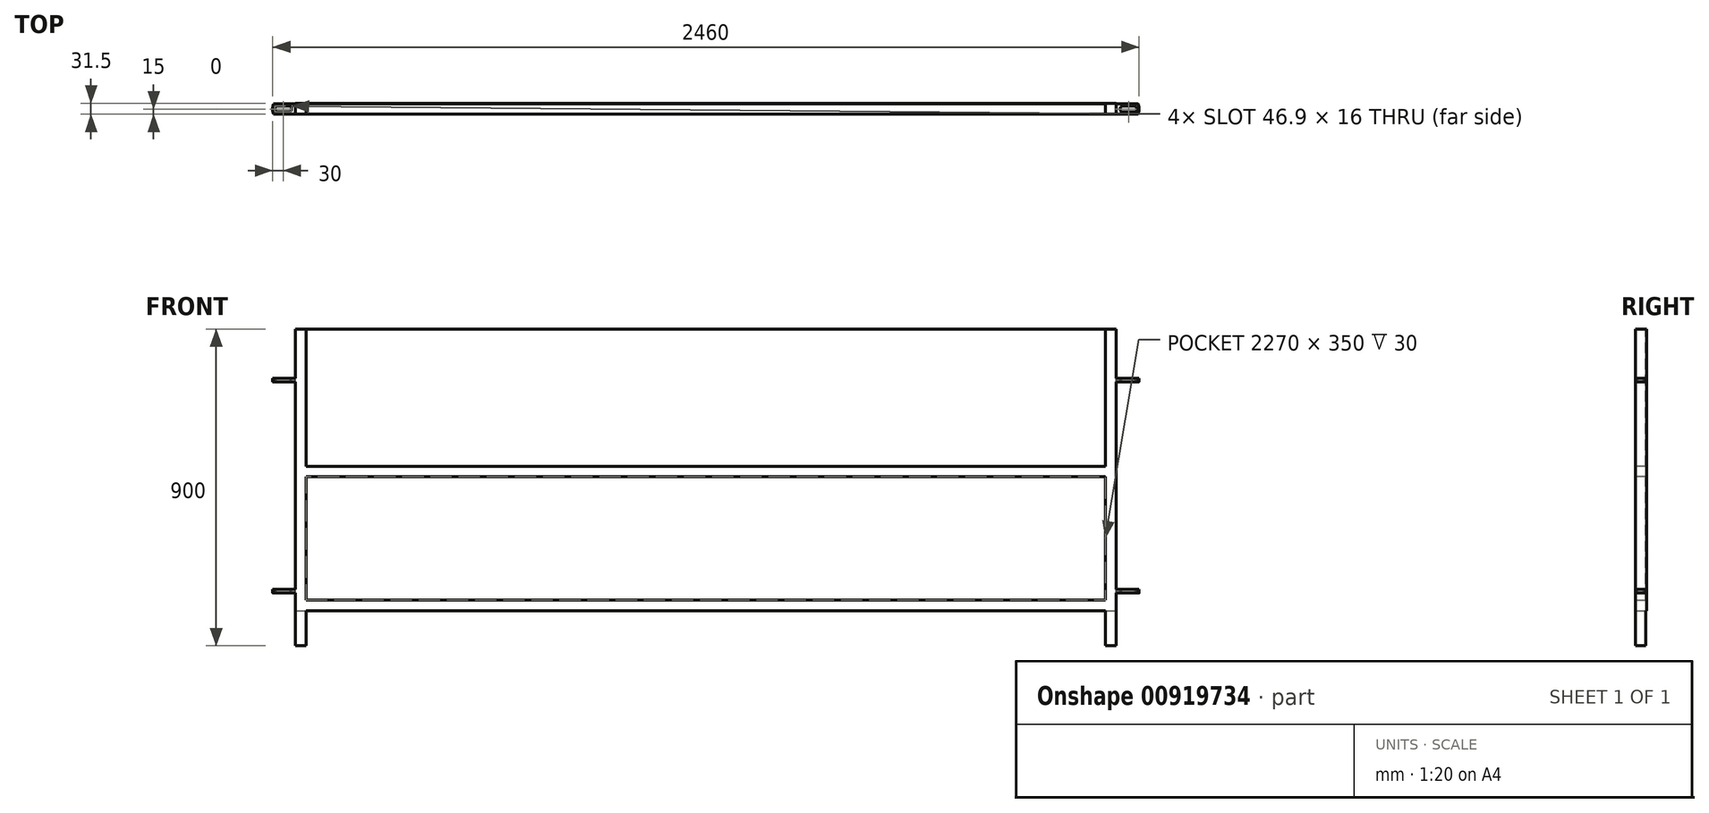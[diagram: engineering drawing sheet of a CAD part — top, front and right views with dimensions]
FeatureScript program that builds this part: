
annotation { "Feature Type Name" : "Feature", "Feature Type Description" : "" }
export const myFeature = defineFeature(function(context is Context, id is Id, definition is map)
    precondition{}
    {
        {
            var Q0;
            Q0=qCreatedBy(makeId("Top.planeOp"),FACE);
            var sketch = newSketch(context, id + "F0", { "sketchPlane" : qUnion([Q0])});
            skLineSegment(sketch, "E0.bottom", {"start": v(-1165, 15) * mm, "end": v(1165, 15) * mm});
            skLineSegment(sketch, "E0.top", {"start": v(-1165, -15) * mm, "end": v(1165, -15) * mm});
            skLineSegment(sketch, "E0.left", {"start": v(-1165, 15) * mm, "end": v(-1165, -15) * mm});
            skLineSegment(sketch, "E0.right", {"start": v(1165, 15) * mm, "end": v(1165, -15) * mm});
            skPoint(sketch, "E0.middle", {"position": v(0, 0) * mm});
            skLineSegment(sketch, "E1", {"start": v(-1135, 15) * mm, "end": v(-1135, -15) * mm});
            skLineSegment(sketch, "E2.MirrorCS", {"start": v(1135, 15) * mm, "end": v(1135, -15) * mm});
            skSolve(sketch);
        }
        {
            var Q0;
            {var subQ0=sQuery(id+"F0.wireOp",EDGE,"E0.left");Q0=makeQuery(id+"F0.imprint","IMPRINT",FACE,{"disambiguationData":[TD([[makeQuery(id+"F0.imprint","IMPRINT",EDGE,{"derivedFrom":subQ0}),1.0]])]});}
            var Q1;
            {var subQ0=sQuery(id+"F0.wireOp",EDGE,"E0.right");Q1=makeQuery(id+"F0.imprint","IMPRINT",FACE,{"disambiguationData":[TD([[makeQuery(id+"F0.imprint","IMPRINT",EDGE,{"derivedFrom":subQ0}),-1.0]])]});}
            extrude(context, id + "F1", {"entities" : qUnion([Q0, Q1]), "oppositeDirection" : true, "depth" : 900 * mm, "offsetDistance" : 25 * mm});
        }
        {
            var Q0;
            Q0=makeQuery(id+"F1.opExtrude","SWEPT_FACE",FACE,{"disambiguationData":[OSD([sQuery(id+"F0.wireOp",EDGE,"E0.right")])]});
            var sketch = newSketch(context, id + "F2", { "sketchPlane" : qUnion([Q0])});
            skLineSegment(sketch, "E3.0.0", {"start": v(15, 0) * mm, "end": v(-15, 0) * mm});
            skLineSegment(sketch, "E3.0.1", {"start": v(-15, 0) * mm, "end": v(-15, -900) * mm});
            skLineSegment(sketch, "E3.0.2", {"start": v(-15, -900) * mm, "end": v(15, -900) * mm});
            skLineSegment(sketch, "E3.0.3", {"start": v(15, -900) * mm, "end": v(15, 0) * mm});
            skLineSegment(sketch, "E4.bottom", {"start": v(-15, 0) * mm, "end": v(15, 0) * mm});
            skLineSegment(sketch, "E4.top", {"start": v(-15, -30) * mm, "end": v(15, -30) * mm});
            skLineSegment(sketch, "E4.left", {"start": v(-15, 0) * mm, "end": v(-15, -30) * mm});
            skLineSegment(sketch, "E4.right", {"start": v(15, 0) * mm, "end": v(15, -30) * mm});
            skLineSegment(sketch, "E5.bottom", {"start": v(15, -390) * mm, "end": v(-15, -390) * mm});
            skLineSegment(sketch, "E5.top", {"start": v(15, -420) * mm, "end": v(-15, -420) * mm});
            skLineSegment(sketch, "E5.left", {"start": v(15, -390) * mm, "end": v(15, -420) * mm});
            skLineSegment(sketch, "E5.right", {"start": v(-15, -390) * mm, "end": v(-15, -420) * mm});
            skLineSegment(sketch, "E6.bottom", {"start": v(-15, -770) * mm, "end": v(15, -770) * mm});
            skLineSegment(sketch, "E6.top", {"start": v(-15, -800) * mm, "end": v(15, -800) * mm});
            skLineSegment(sketch, "E6.left", {"start": v(-15, -770) * mm, "end": v(-15, -800) * mm});
            skLineSegment(sketch, "E6.right", {"start": v(15, -770) * mm, "end": v(15, -800) * mm});
            skSolve(sketch);
        }
        {
            var Q0;
            Q0=makeQuery(id+"F2.imprint","IMPRINT",FACE,{"disambiguationData":[TD([[makeQuery(id+"F2.imprint","IMPRINT",EDGE,{"derivedFrom":sQuery(id+"F2.wireOp",EDGE,"E4.bottom")}),1.0]])]});
            var Q1;
            Q1=makeQuery(id+"F2.imprint","IMPRINT",FACE,{"disambiguationData":[TD([[makeQuery(id+"F2.imprint","IMPRINT",EDGE,{"derivedFrom":sQuery(id+"F2.wireOp",EDGE,"E5.bottom")}),1.0]])]});
            var Q2;
            Q2=makeQuery(id+"F2.imprint","IMPRINT",FACE,{"disambiguationData":[TD([[makeQuery(id+"F2.imprint","IMPRINT",EDGE,{"derivedFrom":sQuery(id+"F2.wireOp",EDGE,"E6.bottom")}),-1.0]])]});
            var Q3;
            Q3=makeQuery(id+"F1.opExtrude","SWEPT_FACE",FACE,{"disambiguationData":[OSD([sQuery(id+"F0.wireOp",EDGE,"E1")])]});
            extrude(context, id + "F3", {"entities" : qUnion([Q0, Q1, Q2]), "operationType" : NewBodyOperationType.ADD, "endBound" : BoundingType.UP_TO_SURFACE, "oppositeDirection" : true, "depth" : 25 * mm, "endBoundEntityFace" : qUnion([Q3]), "offsetDistance" : 25 * mm});
        }
        {
            var Q0;
            Q0=makeQuery(id+"F1.opExtrude","SWEPT_FACE",FACE,{"disambiguationData":[OSD([sQuery(id+"F0.wireOp",EDGE,"E0.right")])]});
            var sketch = newSketch(context, id + "F4", { "sketchPlane" : qUnion([Q0])});
            skLineSegment(sketch, "E7.0.0", {"start": v(15, 0) * mm, "end": v(-15, 0) * mm});
            skLineSegment(sketch, "E7.0.1", {"start": v(-15, 0) * mm, "end": v(-15, -900) * mm});
            skLineSegment(sketch, "E7.0.2", {"start": v(-15, -900) * mm, "end": v(15, -900) * mm});
            skLineSegment(sketch, "E7.0.3", {"start": v(15, -900) * mm, "end": v(15, 0) * mm});
            skLineSegment(sketch, "E8.bottom", {"start": v(-15, -140) * mm, "end": v(15, -140) * mm});
            skLineSegment(sketch, "E8.top", {"start": v(-15, -150) * mm, "end": v(15, -150) * mm});
            skLineSegment(sketch, "E8.left", {"start": v(-15, -140) * mm, "end": v(-15, -150) * mm});
            skLineSegment(sketch, "E8.right", {"start": v(15, -140) * mm, "end": v(15, -150) * mm});
            skLineSegment(sketch, "E9.bottom", {"start": v(-15, -740) * mm, "end": v(15, -740) * mm});
            skLineSegment(sketch, "E9.top", {"start": v(-15, -750) * mm, "end": v(15, -750) * mm});
            skLineSegment(sketch, "E9.left", {"start": v(-15, -740) * mm, "end": v(-15, -750) * mm});
            skLineSegment(sketch, "E9.right", {"start": v(15, -740) * mm, "end": v(15, -750) * mm});
            skSolve(sketch);
        }
        {
            var Q0;
            Q0=makeQuery(id+"F4.imprint","IMPRINT",FACE,{"disambiguationData":[TD([[makeQuery(id+"F4.imprint","IMPRINT",EDGE,{"derivedFrom":sQuery(id+"F4.wireOp",EDGE,"E8.bottom")}),-1.0]])]});
            var Q1;
            Q1=makeQuery(id+"F4.imprint","IMPRINT",FACE,{"disambiguationData":[TD([[makeQuery(id+"F4.imprint","IMPRINT",EDGE,{"derivedFrom":sQuery(id+"F4.wireOp",EDGE,"E9.bottom")}),-1.0]])]});
            extrude(context, id + "F5", {"entities" : qUnion([Q0, Q1]), "depth" : 65 * mm, "offsetDistance" : 25 * mm});
        }
        {
            var Q0;
            Q0=makeQuery(id+"F5.opExtrude","SWEPT_FACE",FACE,{"disambiguationData":[OSD([sQuery(id+"F4.wireOp",EDGE,"E8.bottom")])]});
            var sketch = newSketch(context, id + "F6", { "sketchPlane" : qUnion([Q0])});
            skLineSegment(sketch, "E10.0.0", {"start": v(1165, 15) * mm, "end": v(1165, -15) * mm});
            skLineSegment(sketch, "E10.0.1", {"start": v(1165, -15) * mm, "end": v(1230, -15) * mm});
            skLineSegment(sketch, "E10.0.2", {"start": v(1230, -15) * mm, "end": v(1230, 15) * mm});
            skLineSegment(sketch, "E10.0.3", {"start": v(1230, 15) * mm, "end": v(1165, 15) * mm});
            skLineSegment(sketch, "E11", {"start": v(1230, 0) * mm, "end": v(1165, 0) * mm, "construction": true});
            skLineSegment(sketch, "E12", {"start": v(1180, 0) * mm, "end": v(1180, -8) * mm, "construction": true});
            skLineSegment(sketch, "E13", {"start": v(1180, -8) * mm, "end": v(1180, 8) * mm});
            skPoint(sketch, "E13.endSnap0", {"position": v(1180, -4) * mm});
            skLineSegment(sketch, "E14", {"start": v(1180, 8) * mm, "end": v(1220, 8) * mm});
            skLineSegment(sketch, "E15", {"start": v(1220, 8) * mm, "end": v(1220, -8) * mm});
            skLineSegment(sketch, "E16", {"start": v(1220, -8) * mm, "end": v(1180, -8) * mm});
            skArc(sketch, "E17", {"start": v(1220, -8) * mm, "mid": v(1223.45, 0) * mm, "end": v(1220, 8) * mm});
            skLineSegment(sketch, "E18", {"start": v(1200, 8) * mm, "end": v(1200, 2.91) * mm, "construction": true});
            skArc(sketch, "E19.MirrorCS", {"start": v(1180, -8) * mm, "mid": v(1176.55, 0) * mm, "end": v(1180, 8) * mm});
            skLineSegment(sketch, "E20", {"start": v(1227.36, 15) * mm, "end": v(1227.36, -15) * mm, "construction": true});
            skArc(sketch, "E21", {"start": v(1227.36, -15) * mm, "mid": v(1230, 0) * mm, "end": v(1227.36, 15) * mm});
            skSolve(sketch);
        }
        {
            var Q0;
            {var subQ0=sQuery(id+"F6.wireOp",EDGE,"E10.0.3");var subQ1=sQuery(id+"F6.wireOp",EDGE,"E10.0.2");var subQ2=makeQuery(id+"F6.imprint","INTERSECT",VERTEX,{"derivedFrom":[subQ1,subQ0]});Q0=makeQuery(id+"F6.imprint","IMPRINT",FACE,{"disambiguationData":[TD([[makeQuery(id+"F6.imprint","IMPRINT",EDGE,{"disambiguationData":[TD([[subQ2,1.0]])],"derivedFrom":subQ1}),1.0]])]});}
            var Q1;
            {var subQ0=sQuery(id+"F6.wireOp",EDGE,"E10.0.2");var subQ1=sQuery(id+"F6.wireOp",EDGE,"E10.0.1");var subQ2=makeQuery(id+"F6.imprint","INTERSECT",VERTEX,{"derivedFrom":[subQ1,subQ0]});Q1=makeQuery(id+"F6.imprint","IMPRINT",FACE,{"disambiguationData":[TD([[makeQuery(id+"F6.imprint","IMPRINT",EDGE,{"disambiguationData":[TD([[subQ2,-1.0]])],"derivedFrom":subQ1}),-1.0]])]});}
            var Q2;
            Q2=makeQuery(id+"F6.imprint","IMPRINT",FACE,{"disambiguationData":[TD([[makeQuery(id+"F6.imprint","IMPRINT",EDGE,{"derivedFrom":sQuery(id+"F6.wireOp",EDGE,"E13")}),-1.0]])]});
            var Q3;
            Q3=makeQuery(id+"F6.imprint","IMPRINT",FACE,{"disambiguationData":[TD([[makeQuery(id+"F6.imprint","IMPRINT",EDGE,{"derivedFrom":sQuery(id+"F6.wireOp",EDGE,"E15")}),1.0]])]});
            var Q4;
            Q4=makeQuery(id+"F6.imprint","IMPRINT",FACE,{"disambiguationData":[TD([[makeQuery(id+"F6.imprint","IMPRINT",EDGE,{"derivedFrom":sQuery(id+"F6.wireOp",EDGE,"E13")}),1.0]])]});
            extrude(context, id + "F7", {"entities" : qUnion([Q0, Q1, Q2, Q3, Q4]), "operationType" : NewBodyOperationType.REMOVE, "endBound" : BoundingType.THROUGH_ALL, "oppositeDirection" : true, "depth" : 25 * mm, "offsetDistance" : 25 * mm});
        }
        {
            var Q0;
            Q0=makeQuery(id+"F5.opExtrude","SWEPT_BODY",BODY,{"disambiguationData":[OSD([sQuery(id+"F4.wireOp",EDGE,"E8.bottom"),sQuery(id+"F4.wireOp",EDGE,"E8.top"),sQuery(id+"F4.wireOp",EDGE,"E8.left"),sQuery(id+"F4.wireOp",EDGE,"E8.right")])]});
            var Q1;
            Q1=makeQuery(id+"F5.opExtrude","SWEPT_BODY",BODY,{"disambiguationData":[OSD([sQuery(id+"F4.wireOp",EDGE,"E9.bottom"),sQuery(id+"F4.wireOp",EDGE,"E9.top"),sQuery(id+"F4.wireOp",EDGE,"E9.left"),sQuery(id+"F4.wireOp",EDGE,"E9.right")])]});
            var Q2;
            Q2=qCreatedBy(makeId("Right.planeOp"),FACE);
            mirror(context, id + "F8", {"operationType" : NewBodyOperationType.ADD, "entities" : qUnion([Q0, Q1]), "mirrorPlane" : qUnion([Q2])});
        }
        {
            var Q0;
            {var subQ3=sQuery(id+"F0.wireOp",EDGE,"E0.right");Q0=makeQuery(id+"F8.boolean.opBoolean","SPLIT",FACE,{"disambiguationData":[TD([makeQuery(id+"F5.opExtrude","SWEPT_FACE",FACE,{"disambiguationData":[OSD([sQuery(id+"F4.wireOp",EDGE,"E8.top")])]})])],"derivedFrom":makeQuery(id+"F1.opExtrude","SWEPT_FACE",FACE,{"disambiguationData":[OSD([subQ3])]})});}
            var sketch = newSketch(context, id + "F9", { "sketchPlane" : qUnion([Q0])});
            skLineSegment(sketch, "E22.0", {"start": v(15, -900) * mm, "end": v(15, -800) * mm});
            skLineSegment(sketch, "E23", {"start": v(15, -800) * mm, "end": v(0, -800) * mm, "construction": true});
            skLineSegment(sketch, "E24", {"start": v(15, -800) * mm, "end": v(15, 0) * mm});
            skLineSegment(sketch, "E25", {"start": v(15, 0) * mm, "end": v(16.5, 0) * mm});
            skLineSegment(sketch, "E26", {"start": v(16.5, 0) * mm, "end": v(16.5, -800) * mm});
            skLineSegment(sketch, "E27", {"start": v(16.5, -800) * mm, "end": v(15, -800) * mm});
            skSolve(sketch);
        }
        {
            var Q0;
            {var subQ0=sQuery(id+"F9.wireOp",EDGE,"E25");Q0=makeQuery(id+"F9.imprint","IMPRINT",FACE,{"disambiguationData":[TD([[makeQuery(id+"F9.imprint","IMPRINT",EDGE,{"derivedFrom":subQ0}),-1.0]])]});}
            var Q1;
            {var subQ0=sQuery(id+"F0.wireOp",EDGE,"E0.left");Q1=makeQuery(id+"F8.boolean.opBoolean","SPLIT",FACE,{"disambiguationData":[TD([makeQuery(id+"F8.opPattern","COPY",FACE,{"derivedFrom":makeQuery(id+"F5.opExtrude","SWEPT_FACE",FACE,{"disambiguationData":[OSD([sQuery(id+"F4.wireOp",EDGE,"E8.top")])]}),"instanceName":"1"})])],"derivedFrom":makeQuery(id+"F1.opExtrude","SWEPT_FACE",FACE,{"disambiguationData":[OSD([subQ0])]})});}
            extrude(context, id + "F10", {"entities" : qUnion([Q0]), "operationType" : NewBodyOperationType.ADD, "endBound" : BoundingType.UP_TO_SURFACE, "oppositeDirection" : true, "depth" : 25 * mm, "endBoundEntityFace" : qUnion([Q1]), "offsetDistance" : 25 * mm});
        }
    });
